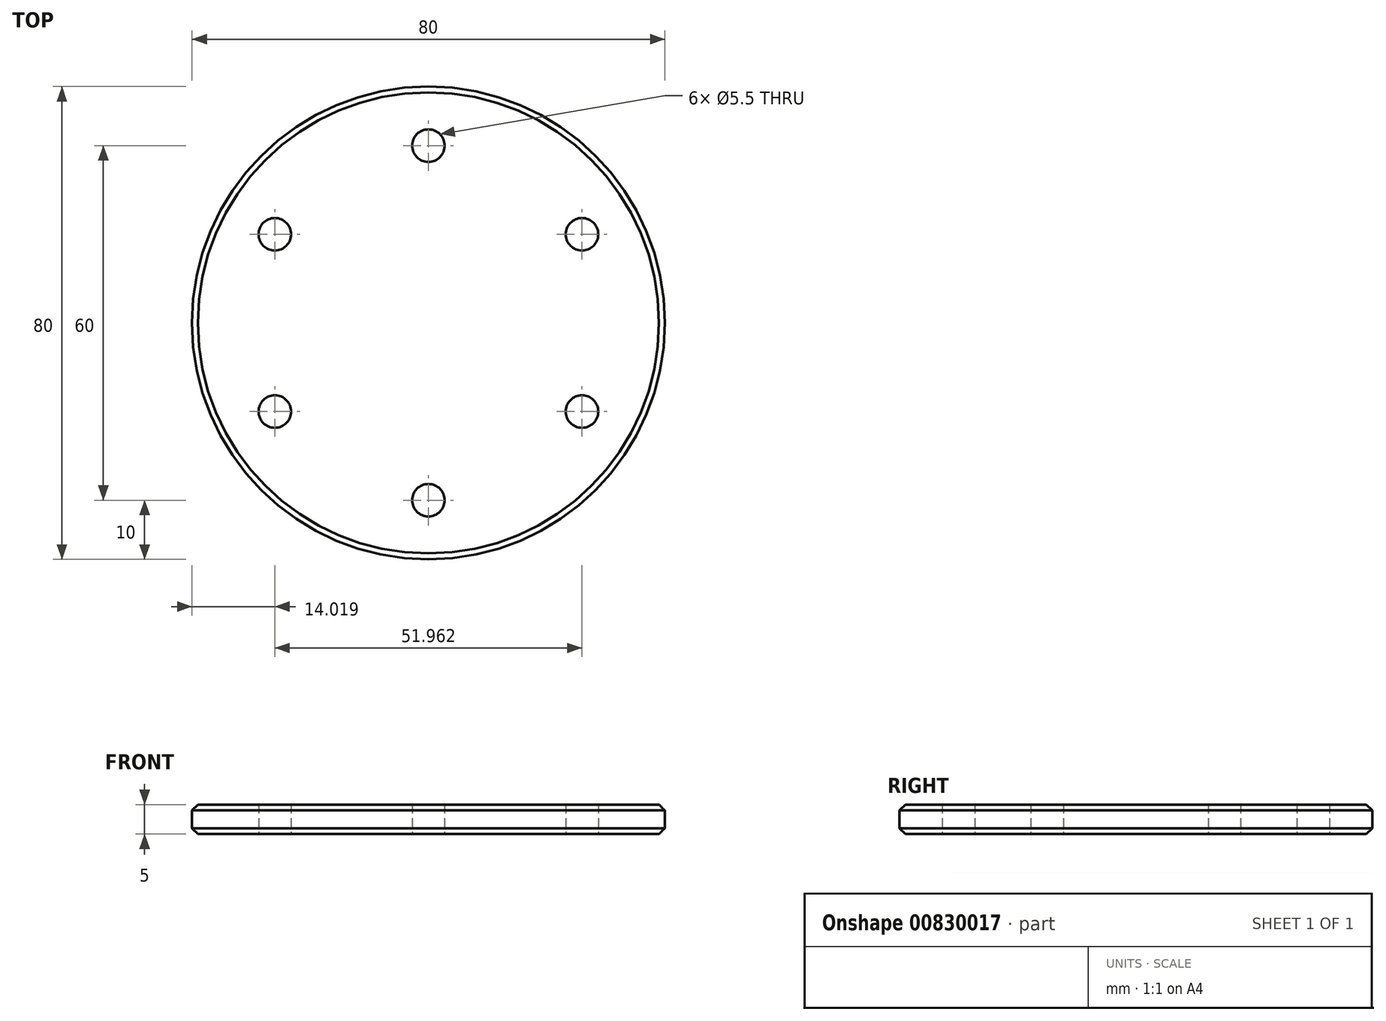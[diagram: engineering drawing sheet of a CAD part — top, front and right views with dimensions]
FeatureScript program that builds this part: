
annotation { "Feature Type Name" : "Feature", "Feature Type Description" : "" }
export const myFeature = defineFeature(function(context is Context, id is Id, definition is map)
    precondition{}
    {
        {
            var Q0;
            Q0=qCreatedBy(makeId("Top.planeOp"),FACE);
            var sketch = newSketch(context, id + "F0", { "sketchPlane" : qUnion([Q0])});
            skCircle(sketch, "E0", {"center": v(0, 0) * mm, "radius": 40 * mm});
            skSolve(sketch);
        }
        {
            var Q0;
            Q0=makeQuery(id+"F0.imprint","IMPRINT",FACE,{"disambiguationData":[TD([[makeQuery(id+"F0.imprint","IMPRINT",EDGE,{"derivedFrom":sQuery(id+"F0.wireOp",EDGE,"E0")}),1.0]])]});
            extrude(context, id + "F1", {"entities" : qUnion([Q0]), "depth" : 5 * mm, "offsetDistance" : 25 * mm});
        }
        {
            var Q0;
            Q0=makeQuery(id+"F1.opExtrude","CAP_FACE",FACE,{"disambiguationData":[OSD([sQuery(id+"F0.wireOp",EDGE,"E0")])],"isStart":true});
            var sketch = newSketch(context, id + "F2", { "sketchPlane" : qUnion([Q0])});
            skCircle(sketch, "E1", {"center": v(0, 0) * mm, "radius": 30 * mm, "construction": true});
            skPoint(sketch, "E2", {"position": v(0, 30) * mm});
            skLineSegment(sketch, "E3", {"start": v(0, 0) * mm, "end": v(0, 30) * mm, "construction": true});
            skLineSegment(sketch, "E4", {"start": v(0, 0) * mm, "end": v(25.98, -15) * mm, "construction": true});
            skLineSegment(sketch, "E5", {"start": v(-25.98, -15) * mm, "end": v(0, 0) * mm, "construction": true});
            skLineSegment(sketch, "E6", {"start": v(0, 0) * mm, "end": v(0, -30) * mm, "construction": true});
            skLineSegment(sketch, "E7", {"start": v(0, 0) * mm, "end": v(-25.98, 15) * mm, "construction": true});
            skLineSegment(sketch, "E8", {"start": v(0, 0) * mm, "end": v(25.98, 15) * mm, "construction": true});
            skSolve(sketch);
        }
        {
            var Q0;
            Q0=sQuery(id+"F2.wireOp",VERTEX,"E2");
            var Q1;
            Q1=sQuery(id+"F2.wireOp",VERTEX,"E4.end");
            var Q2;
            Q2=sQuery(id+"F2.wireOp",VERTEX,"E5.start");
            var Q3;
            Q3=sQuery(id+"F2.wireOp",VERTEX,"E6.end");
            var Q4;
            Q4=sQuery(id+"F2.wireOp",VERTEX,"E8.end");
            var Q5;
            Q5=sQuery(id+"F2.wireOp",VERTEX,"E7.end");
            var Q6;
            Q6=makeQuery(id+"F1.opExtrude","SWEPT_BODY",BODY,{"disambiguationData":[OSD([sQuery(id+"F0.wireOp",EDGE,"E0")])]});
            hole(context, id + "F3", {"style" : HoleStyle.SIMPLE, "endStyle" : HoleEndStyle.THROUGH, "holeDiameter" : 5.5 * mm, "majorDiameter" : 5 * mm, "isTappedThrough" : true, "tappedDepth" : 12 * mm, "tapClearance" : 3, "locations" : qUnion([Q0, Q1, Q2, Q3, Q4, Q5]), "scope" : qUnion([Q6])});
        }
        {
            var Q0;
            Q0=makeQuery(id+"F1.opExtrude","CAP_EDGE",EDGE,{"disambiguationData":[OSD([sQuery(id+"F0.wireOp",EDGE,"E0")])],"isStart":false});
            var Q1;
            Q1=makeQuery(id+"F1.opExtrude","CAP_EDGE",EDGE,{"disambiguationData":[OSD([sQuery(id+"F0.wireOp",EDGE,"E0")])],"isStart":true});
            chamfer(context, id + "F4", {"entities" : qUnion([Q0, Q1]), "width" : 1 * mm, "tangentPropagation" : true});
        }
    });
